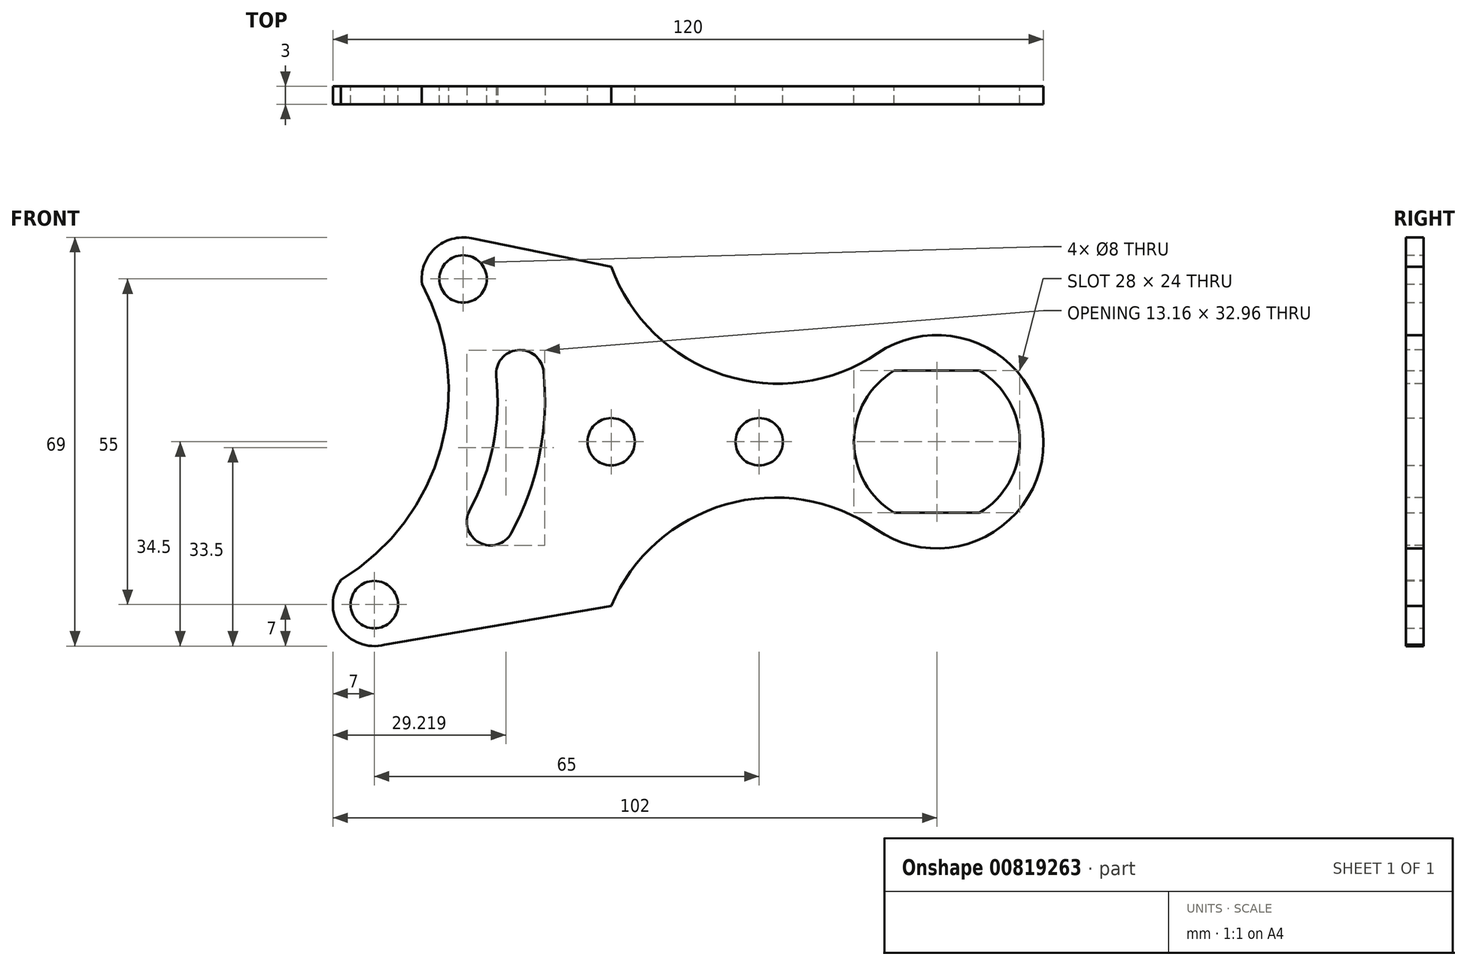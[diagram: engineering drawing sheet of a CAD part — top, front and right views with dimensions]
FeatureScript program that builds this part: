
annotation { "Feature Type Name" : "Feature", "Feature Type Description" : "" }
export const myFeature = defineFeature(function(context is Context, id is Id, definition is map)
    precondition{}
    {
        {
            var Q0;
            Q0=qCreatedBy(makeId("Front.planeOp"),FACE);
            var sketch = newSketch(context, id + "F0", { "sketchPlane" : qUnion([Q0])});
            skLineSegment(sketch, "E0", {"start": v(-34.57, 34.36) * mm, "end": v(47.08, 17.74) * mm});
            skLineSegment(sketch, "E1", {"start": v(-49.22, -34.28) * mm, "end": v(47.08, -17.74) * mm});
            skArc(sketch, "E2", {"start": v(47.08, -17.74) * mm, "mid": v(62.03, 0) * mm, "end": v(47.08, 17.74) * mm});
            skArc(sketch, "E3", {"start": v(-34.57, 34.36) * mm, "mid": v(-40.73, 32.63) * mm, "end": v(-42.92, 26.62) * mm});
            skArc(sketch, "E4", {"start": v(-56.58, -23.32) * mm, "mid": v(-56.78, -31.4) * mm, "end": v(-49.22, -34.28) * mm});
            skLineSegment(sketch, "E5", {"start": v(68.71, 0) * mm, "end": v(-71.53, 0) * mm, "construction": true});
            skCircle(sketch, "E6", {"center": v(-35.97, 27.5) * mm, "radius": 4 * mm});
            skCircle(sketch, "E7", {"center": v(-50.97, -27.5) * mm, "radius": 4 * mm});
            skArc(sketch, "E8", {"start": v(36.82, 12) * mm, "mid": v(30.03, 0) * mm, "end": v(36.82, -12) * mm});
            skCircle(sketch, "E9", {"center": v(-10.97, 0) * mm, "radius": 4 * mm});
            skCircle(sketch, "E10", {"center": v(14.03, 0) * mm, "radius": 4 * mm});
            skArc(sketch, "E11", {"start": v(-56.58, -23.32) * mm, "mid": v(-39.75, -1.08) * mm, "end": v(-42.92, 26.62) * mm});
            skLineSegment(sketch, "E12", {"start": v(36.82, 12) * mm, "end": v(51.24, 12) * mm});
            skLineSegment(sketch, "E13", {"start": v(36.82, -12) * mm, "end": v(51.24, -12) * mm});
            skArc(sketch, "E14.trimOffspring", {"start": v(51.24, -12) * mm, "mid": v(58.03, 0) * mm, "end": v(51.24, 12) * mm});
            skSolve(sketch);
        }
        {
            var Q0;
            Q0=makeQuery(id+"F0.imprint","IMPRINT",FACE,{"disambiguationData":[TD([[makeQuery(id+"F0.imprint","IMPRINT",EDGE,{"derivedFrom":sQuery(id+"F0.wireOp",EDGE,"E0")}),-1.0]])]});
            extrude(context, id + "F1", {"entities" : qUnion([Q0]), "depth" : 3 * mm, "offsetDistance" : 25 * mm});
        }
        {
            var Q0;
            Q0=makeQuery(id+"F1.opExtrude","CAP_FACE",FACE,{"disambiguationData":[OSD([sQuery(id+"F0.wireOp",EDGE,"E0"),sQuery(id+"F0.wireOp",EDGE,"E1"),sQuery(id+"F0.wireOp",EDGE,"E2"),sQuery(id+"F0.wireOp",EDGE,"E3"),sQuery(id+"F0.wireOp",EDGE,"E4"),sQuery(id+"F0.wireOp",EDGE,"ro7dAiLE-VOUL-hYEq-clKP-LcByFZGLVR4N"),sQuery(id+"F0.wireOp",EDGE,"E6"),sQuery(id+"F0.wireOp",EDGE,"E7"),sQuery(id+"F0.wireOp",EDGE,"E8")])],"isStart":false});
            var sketch = newSketch(context, id + "F2", { "sketchPlane" : qUnion([Q0])});
            skLineSegment(sketch, "E15", {"start": v(44.03, 0) * mm, "end": v(44.03, 50.8) * mm, "construction": true});
            skArc(sketch, "E16", {"start": v(33.76, -14.78) * mm, "mid": v(62.03, -0.13) * mm, "end": v(33.98, 14.93) * mm});
            skArc(sketch, "E17", {"start": v(-10.97, 29.56) * mm, "mid": v(7.94, 11.29) * mm, "end": v(33.98, 14.93) * mm});
            skArc(sketch, "E18", {"start": v(33.76, -14.78) * mm, "mid": v(8.32, -10.6) * mm, "end": v(-10.97, -27.7) * mm});
            skLineSegment(sketch, "E19", {"start": v(-10.97, 0) * mm, "end": v(-10.97, 38.47) * mm, "construction": true});
            skLineSegment(sketch, "E20", {"start": v(-10.97, 0) * mm, "end": v(-10.97, -32.7) * mm, "construction": true});
            skLineSegment(sketch, "E21.0", {"start": v(-10.97, 29.56) * mm, "end": v(47.08, 17.74) * mm});
            skLineSegment(sketch, "E22.0", {"start": v(-10.97, -27.7) * mm, "end": v(47.08, -17.74) * mm});
            skPoint(sketch, "E23", {"position": v(-60.99, 9.9) * mm});
            skArc(sketch, "E24", {"start": v(-34.87, -11.6) * mm, "mid": v(-30.9, -0.6) * mm, "end": v(-30.36, 11.08) * mm});
            skArc(sketch, "E25", {"start": v(-22.4, 11.92) * mm, "mid": v(-26.8, 15.48) * mm, "end": v(-30.36, 11.08) * mm});
            skArc(sketch, "E26", {"start": v(-34.87, -11.6) * mm, "mid": v(-33.26, -17.02) * mm, "end": v(-27.84, -15.4) * mm});
            skPoint(sketch, "E27.orphan", {"position": v(-35.97, 27.5) * mm});
            skPoint(sketch, "E28.orphan", {"position": v(-50.97, -27.5) * mm});
            skArc(sketch, "E29.trimOffspring", {"start": v(-27.84, -15.4) * mm, "mid": v(-23.05, -2.16) * mm, "end": v(-22.4, 11.92) * mm});
            skSolve(sketch);
        }
        {
            var Q0;
            Q0 = qSketchRegion(id + "F2", true);
            var Q1;
            {var subQ0=sQuery(id+"F2.wireOp",EDGE,"ZDbQ7vL0-dDcV-GmUL-GDL3-JwqfCfdRMKUh");Q1=makeQuery(id+"F2.imprint","IMPRINT",FACE,{"disambiguationData":[TD([[makeQuery(id+"F2.imprint","IMPRINT",EDGE,{"derivedFrom":subQ0}),1.0]])]});}
            var Q2;
            {var subQ0=sQuery(id+"F2.wireOp",EDGE,"9vmtxHc3-44XT-wuqZ-OUij-3fkULDJmHdvC");Q2=makeQuery(id+"F2.imprint","IMPRINT",FACE,{"disambiguationData":[TD([[makeQuery(id+"F2.imprint","IMPRINT",EDGE,{"derivedFrom":subQ0}),1.0]])]});}
            var Q3;
            {var subQ0=sQuery(id+"F2.wireOp",EDGE,"286b04a8-ccac-4efb-a794-6075400b3d8e");Q3=makeQuery(id+"F2.imprint","IMPRINT",FACE,{"disambiguationData":[TD([[makeQuery(id+"F2.imprint","IMPRINT",EDGE,{"derivedFrom":subQ0}),1.0]])]});}
            extrude(context, id + "F3", {"entities" : qUnion([Q0, Q1, Q2, Q3]), "operationType" : NewBodyOperationType.REMOVE, "oppositeDirection" : true, "depth" : 25 * mm, "offsetDistance" : 25 * mm});
        }
    });
